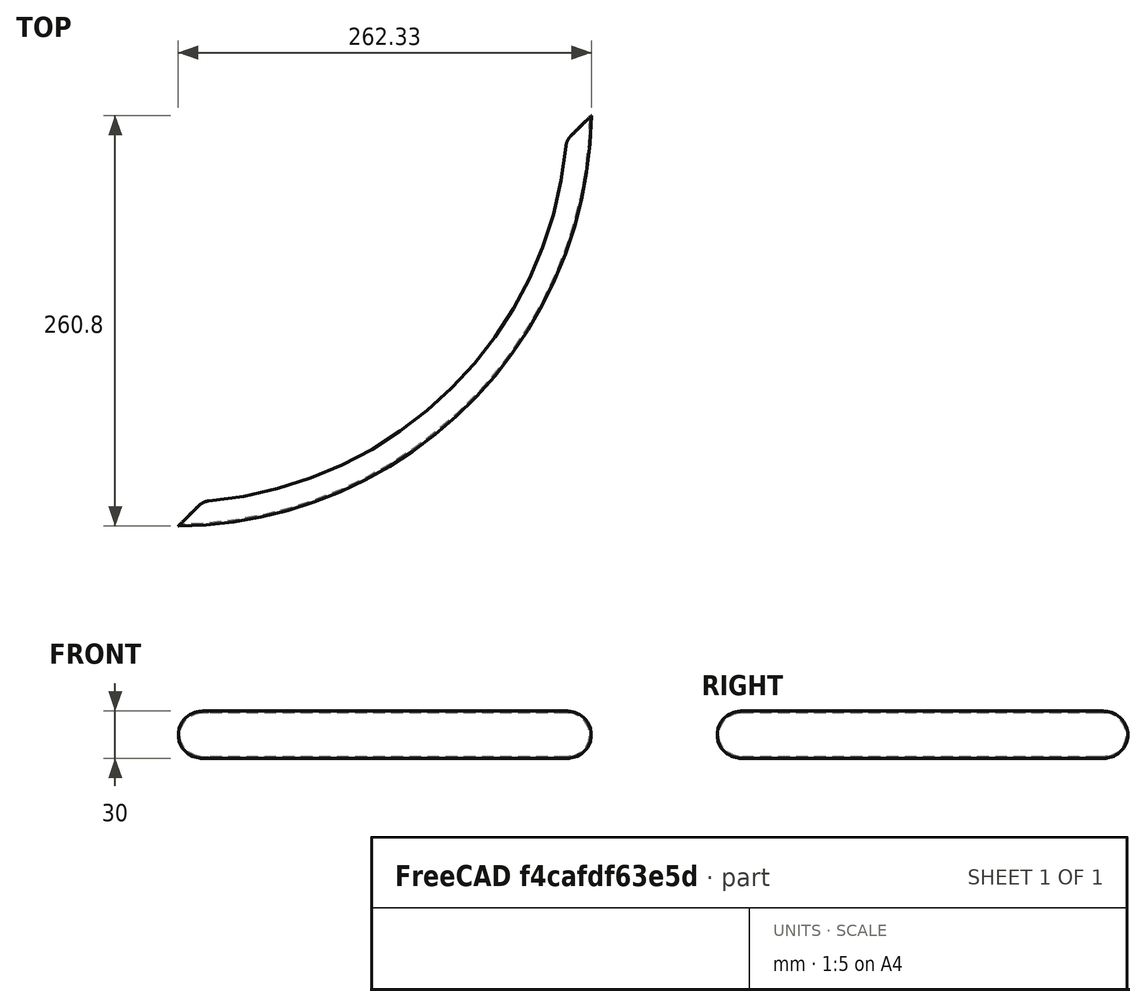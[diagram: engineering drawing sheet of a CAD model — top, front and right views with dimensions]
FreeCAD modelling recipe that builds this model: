
FCSTD DOCUMENT  (FreeCAD 0.16R)
Label: Mudguard2
License: All rights reserved
LicenseURL: http://en.wikipedia.org/wiki/All_rights_reserved
objects: Sketcher::SketchObject×4, PartDesign::Revolution×1, PartDesign::Pad×1, Part::Cut×1, PartDesign::Fillet×1, Mesh::Feature×1
note: 10 computed .brp shape members not serialized (recipe doc carries the construction recipe); baked Part::Feature solids carry a one-line shape summary decoded from their .brp

FEATURE [Sketcher::SketchObject] Sketch001
  Placement = pos=(0,0,0) rot=(1,0,0;1.5708rad)
  sketch-geometry (4):
    g0: ArcOfCircle CenterX=250 CenterY=0 CenterZ=0 NormalX=0 NormalY=0 NormalZ=1 Radius=15 StartAngle=4.71239 EndAngle=7.85398
    g1: ArcOfCircle CenterX=250 CenterY=0 CenterZ=0 NormalX=0 NormalY=0 NormalZ=1 Radius=14 StartAngle=4.71239 EndAngle=7.85398
    g2: LineSegment StartX=250 StartY=15 StartZ=0 EndX=250 EndY=14 EndZ=0
    g3: LineSegment StartX=250 StartY=-15 StartZ=0 EndX=250 EndY=-14 EndZ=0
  constraints (13):
    c: DistanceX(g0,g-1) = -250
    c: Radius(g0) = 15
    c: PointOnObject(g0,g-1)
    c: Symmetric(g0,g0,g0)
    c: Coincident(g1,g0)
    c: Radius(g1) = 14
    c: DistanceX(g1) = 250
    c: DistanceX(g1) = 250
    c: Coincident(g2,g0)
    c: Coincident(g2,g1)
    c: Vertical(g2)
    c: Coincident(g3,g0)
    c: Coincident(g3,g1)
FEATURE [PartDesign::Revolution] Revolution
  Angle = 90
  Axis = (0,0,1)
  Base = (0,0,0)
  Placement = pos=(0,0,0) rot=(1,0,0;1.5708rad)
  ReferenceAxis = -> Sketch001 [V_Axis]
  Reversed = true
  Sketch = -> Sketch001
FEATURE [Sketcher::SketchObject] Sketch002
  sketch-geometry (3):
    g0: LineSegment StartX=307.15 StartY=37.7434 StartZ=0 EndX=-27.9422 EndY=-295.389 EndZ=0
    g1: LineSegment StartX=-27.9422 StartY=-295.389 StartZ=0 EndX=4.8812 EndY=80.7716 EndZ=0
    g2: LineSegment StartX=4.8812 StartY=80.7716 StartZ=0 EndX=307.15 EndY=37.7434 EndZ=0
  constraints (9):
    c: Coincident(g0,g1)
    c: Coincident(g1,g2)
    c: Coincident(g2,g0)
    c: DistanceX(g0) = 307.15
    c: DistanceY(g0) = 37.7434
    c: DistanceY(g0) = -295.389
    c: DistanceX(g0) = -27.9422
    c: Distance(g1) = 377.59
    c: Distance(g2) = 305.316
FEATURE [PartDesign::Pad] Pad
  Length = 40
  Length2 = 100
  Midplane = true
  Sketch = -> Sketch002
  Type = 0
FEATURE [Part::Cut] Cut
  Base = -> Revolution
  Tool = -> Pad
FEATURE [PartDesign::Fillet] Fillet
  Base = -> Cut [Edge7,Edge5,Edge11,Edge9]
  Radius = 10
FEATURE [Mesh::Feature] Mesh  label="Fillet (Meshed)"
FEATURE [Sketcher::SketchObject] Sketch
  Placement = pos=(0,0,0) rot=(-1,0,0;4.71239rad)
FEATURE [Sketcher::SketchObject] Sketch003
  sketch-geometry (1):
    g0: LineSegment [constr] StartX=0 StartY=0 StartZ=0 EndX=352.954 EndY=-420.634 EndZ=0
  constraints (2):
    c: Coincident(g0,g-1)
    c: Angle(g0) = -0.872665
